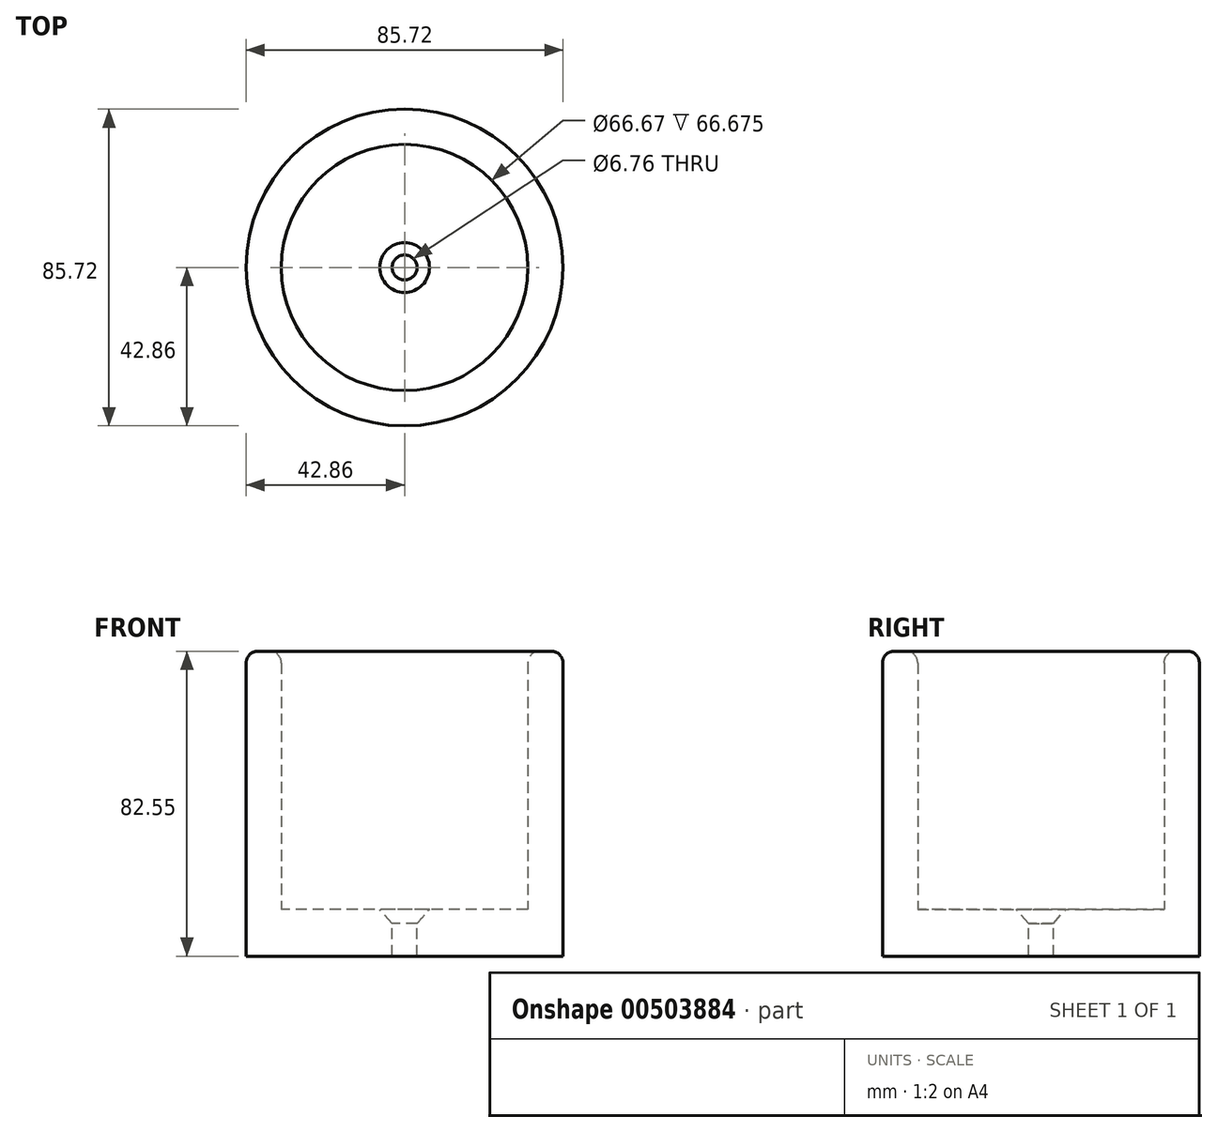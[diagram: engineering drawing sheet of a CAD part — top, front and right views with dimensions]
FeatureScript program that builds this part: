
annotation { "Feature Type Name" : "Feature", "Feature Type Description" : "" }
export const myFeature = defineFeature(function(context is Context, id is Id, definition is map)
    precondition{}
    {
        {
            var Q0;
            Q0=qCreatedBy(makeId("Top.planeOp"),FACE);
            var sketch = newSketch(context, id + "F0", { "sketchPlane" : qUnion([Q0])});
            skCircle(sketch, "E0", {"center": v(0, 0) * mm, "radius": 33.34 * mm});
            skCircle(sketch, "E1", {"center": v(0, 0) * mm, "radius": 42.86 * mm});
            skSolve(sketch);
        }
        {
            var Q0;
            Q0 = qSketchRegion(id + "F0", true);
            extrude(context, id + "F1", {"entities" : qUnion([Q0]), "depth" : 69.85 * mm});
        }
        {
            var Q0;
            Q0=makeQuery(id+"F1.opExtrude","CAP_FACE",FACE,{"disambiguationData":[OSD([sQuery(id+"F0.wireOp",EDGE,"E0"),sQuery(id+"F0.wireOp",EDGE,"E1")])],"isStart":true});
            var sketch = newSketch(context, id + "F2", { "sketchPlane" : qUnion([Q0])});
            skCircle(sketch, "E2.0", {"center": v(0, 0) * mm, "radius": 42.86 * mm});
            skSolve(sketch);
        }
        {
            var Q0;
            Q0 = qSketchRegion(id + "F2", true);
            extrude(context, id + "F3", {"entities" : qUnion([Q0]), "operationType" : NewBodyOperationType.ADD, "depth" : 12.7 * mm});
        }
        {
            var Q0;
            Q0=makeQuery(id+"F3.opExtrude","CAP_FACE",FACE,{"disambiguationData":[OSD([sQuery(id+"F2.wireOp",EDGE,"E2.0")])],"isStart":true});
            var sketch = newSketch(context, id + "F4", { "sketchPlane" : qUnion([Q0])});
            skPoint(sketch, "E3", {"position": v(0, 0) * mm});
            skSolve(sketch);
        }
        {
            var Q0;
            Q0=sQuery(id+"F4.wireOp",VERTEX,"E3");
            var Q1;
            Q1=makeQuery(id+"F1.opExtrude","SWEPT_BODY",BODY,{"disambiguationData":[OSD([sQuery(id+"F0.wireOp",EDGE,"E0"),sQuery(id+"F0.wireOp",EDGE,"E1")])]});
            hole(context, id + "F5", {"style" : HoleStyle.C_SINK, "endStyle" : HoleEndStyle.THROUGH, "standardTappedOrClearance" : lookupTablePath({ "standard" : "ANSI", "fit" : "Normal (ASME)", "size" : "1/4", "type" : "Clearance" }), "standardBlindInLast" : lookupTablePath({ "fit" : "Free", "standard" : "ANSI", "size" : "1/4", "type" : "Clearance" }), "holeDiameter" : 6.76 * mm, "cSinkDiameter" : 13.5 * mm, "cSinkAngle" : 82 * degree, "isTappedThrough" : true, "tappedDepth" : 12.7 * mm, "tapClearance" : 3, "locations" : qUnion([Q0]), "scope" : qUnion([Q1])});
        }
        {
            var Q0;
            Q0=makeQuery(id+"F1.opExtrude","CAP_EDGE",EDGE,{"disambiguationData":[OSD([sQuery(id+"F0.wireOp",EDGE,"E0")])],"isStart":true});
            var Q1;
            Q1=makeQuery(id+"F1.opExtrude","CAP_EDGE",EDGE,{"disambiguationData":[OSD([sQuery(id+"F0.wireOp",EDGE,"E0")])],"isStart":false});
            var Q2;
            Q2=makeQuery(id+"F1.opExtrude","CAP_EDGE",EDGE,{"disambiguationData":[OSD([sQuery(id+"F0.wireOp",EDGE,"E1")])],"isStart":false});
            fillet(context, id + "F6", {"entities" : qUnion([Q0, Q1, Q2]), "radius" : 3.17 * mm, "tangentPropagation" : true, "allowEdgeOverflow" : false});
        }
    });
